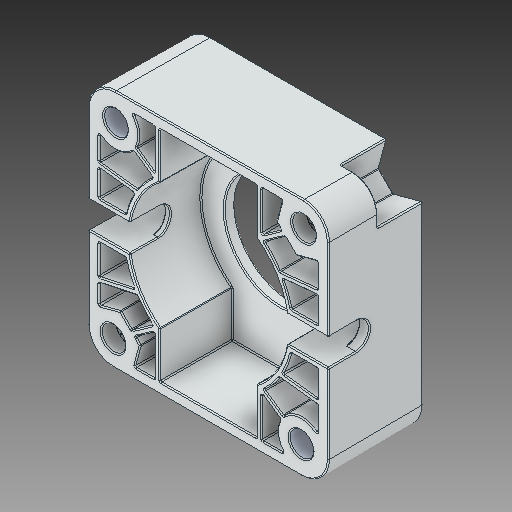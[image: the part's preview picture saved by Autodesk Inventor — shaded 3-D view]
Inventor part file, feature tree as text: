
AUTODESK INVENTOR PART (.ipt)
format: ipt  version: 2018 (Build 220112000, 112)  size: 1,381,376 bytes
history: native  units: in
note: dims shown in document units (in); Inventor stores cm internally (conversion verified against a paired STEP export)
features: fillet x1
ambient origin geometry x8: Origin, YZ Plane, XZ Plane, XY Plane, X Axis, Y Axis, Z Axis, Center Point
bodies: Solid1 (feature_tree)
feature tree (1):
  fillet  "Fillet7"  [1 undecoded]
note: 1 required parameter value undecoded (feature->parameter linkage not recoverable at this tier; creation-order binding heuristic only, values carry confidence <= 0.55)
